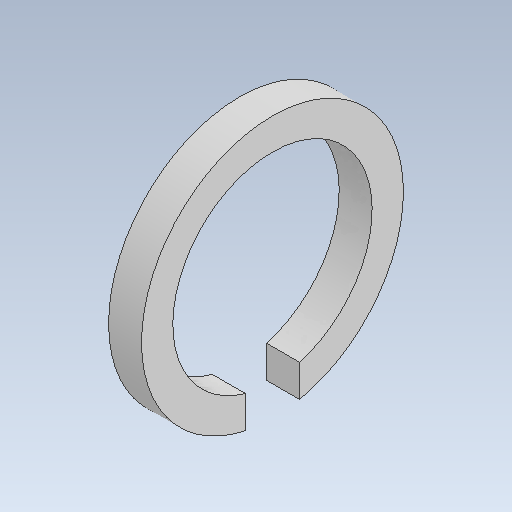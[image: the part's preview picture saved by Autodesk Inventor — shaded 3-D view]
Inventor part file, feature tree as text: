
AUTODESK INVENTOR PART (.ipt)
format: ipt  version: 2021 (Build 250183000, 183)  size: 123,904 bytes
history: native  units: mm
features: extrude x2, sketch x2
ambient origin geometry x8: Origin, YZ Plane, XZ Plane, XY Plane, X Axis, Y Axis, Z Axis, Center Point
bodies: Solid1 (feature_tree)
feature tree (4):
  extrude  "Extrusion1"  Depth=9.5mm
  extrude  "Extrusion2"  Depth=10.0mm
  sketch  "Sketch1"  dims[d0=60.5mm d1=9.5mm]
  sketch  "Sketch2"  dims[d2=10.0mm d3=0.0mm d4=8.218012mm d5=8.218012mm d6=10.0mm d7=0.0mm]
